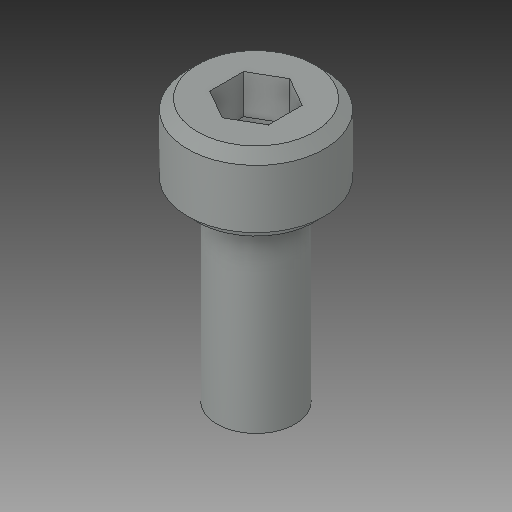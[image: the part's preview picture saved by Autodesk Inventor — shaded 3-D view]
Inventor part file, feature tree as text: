
AUTODESK INVENTOR PART (.ipt)
format: ipt  version: 2018 (Build 220112000, 112)  size: 106,496 bytes
history: native  units: in
note: dims shown in document units (in); Inventor stores cm internally (conversion verified against a paired STEP export)
features: chamfer x1
ambient origin geometry x8: Origin, YZ Plane, XZ Plane, XY Plane, X Axis, Y Axis, Z Axis, Center Point
bodies: Solid1 (feature_tree)
feature tree (1):
  chamfer  "Chamfer2"  [1 undecoded]
note: 1 required parameter value undecoded (feature->parameter linkage not recoverable at this tier; creation-order binding heuristic only, values carry confidence <= 0.55)
